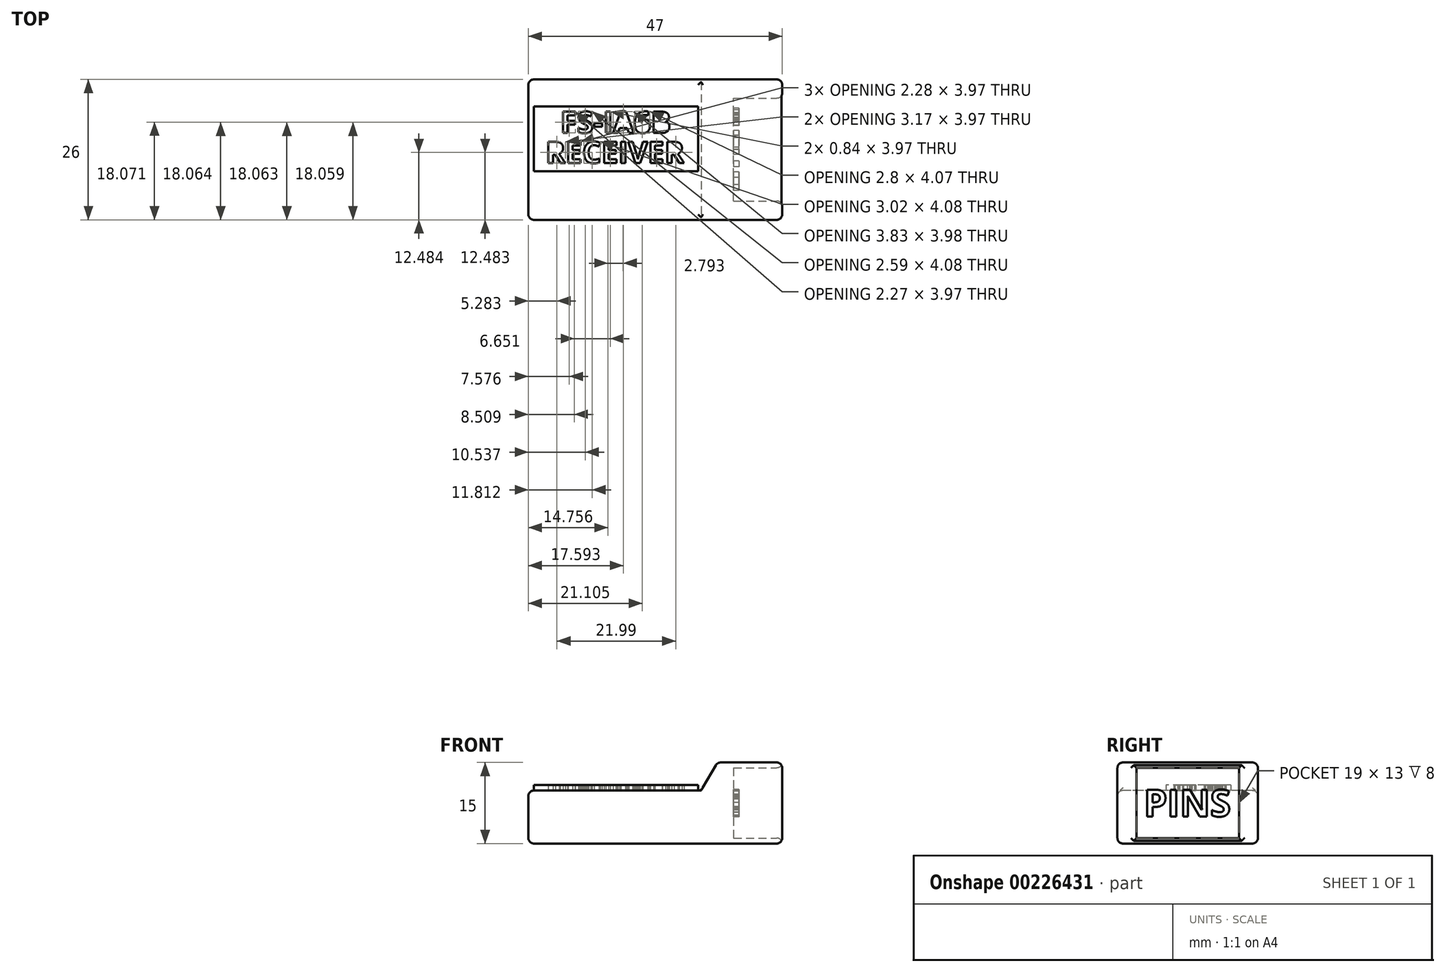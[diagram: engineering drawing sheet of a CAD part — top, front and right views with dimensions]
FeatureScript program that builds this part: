
annotation { "Feature Type Name" : "Feature", "Feature Type Description" : "" }
export const myFeature = defineFeature(function(context is Context, id is Id, definition is map)
    precondition{}
    {
        {
            var Q0;
            Q0=qCreatedBy(makeId("Front.planeOp"),FACE);
            var sketch = newSketch(context, id + "F0", { "sketchPlane" : qUnion([Q0])});
            skLineSegment(sketch, "E0.bottom", {"start": v(0, 0) * mm, "end": v(47, 0) * mm});
            skLineSegment(sketch, "E0.top", {"start": v(0, -15) * mm, "end": v(47, -15) * mm});
            skLineSegment(sketch, "E0.left", {"start": v(0, 0) * mm, "end": v(0, -15) * mm});
            skLineSegment(sketch, "E0.right", {"start": v(47, 0) * mm, "end": v(47, -15) * mm});
            skSolve(sketch);
        }
        {
            var Q0;
            Q0=makeQuery(id+"F0.imprint","IMPRINT",FACE,{"disambiguationData":[TD([[makeQuery(id+"F0.imprint","IMPRINT",EDGE,{"derivedFrom":sQuery(id+"F0.wireOp",EDGE,"E0.bottom")}),-1.0]])]});
            extrude(context, id + "F1", {"entities" : qUnion([Q0]), "depth" : 26 * mm, "offsetDistance" : 25.4 * mm});
        }
        {
            var Q0;
            Q0=makeQuery(id+"F1.opExtrude","CAP_FACE",FACE,{"disambiguationData":[OSD([sQuery(id+"F0.wireOp",EDGE,"E0.bottom"),sQuery(id+"F0.wireOp",EDGE,"E0.top"),sQuery(id+"F0.wireOp",EDGE,"E0.left"),sQuery(id+"F0.wireOp",EDGE,"E0.right")])],"isStart":false});
            var sketch = newSketch(context, id + "F2", { "sketchPlane" : qUnion([Q0])});
            skLineSegment(sketch, "E1", {"start": v(0, -5.2) * mm, "end": v(32, -5.2) * mm});
            skLineSegment(sketch, "E2", {"start": v(32, -5.2) * mm, "end": v(35, 0) * mm});
            skSolve(sketch);
        }
        {
            var Q0;
            {var subQ0=sQuery(id+"F2.wireOp",EDGE,"E1");Q0=makeQuery(id+"F2.imprint","IMPRINT",FACE,{"disambiguationData":[TD([[makeQuery(id+"F2.imprint","IMPRINT",EDGE,{"derivedFrom":subQ0}),1.0]])]});}
            extrude(context, id + "F3", {"entities" : qUnion([Q0]), "operationType" : NewBodyOperationType.REMOVE, "endBound" : BoundingType.THROUGH_ALL, "oppositeDirection" : true, "depth" : 25.4 * mm, "offsetDistance" : 25.4 * mm});
        }
        {
            var Q0;
            Q0=makeQuery(id+"F1.opExtrude","SWEPT_FACE",FACE,{"disambiguationData":[OSD([sQuery(id+"F0.wireOp",EDGE,"E0.right")])]});
            var sketch = newSketch(context, id + "F4", { "sketchPlane" : qUnion([Q0])});
            skLineSegment(sketch, "E3.bottom", {"start": v(-22.5, -1) * mm, "end": v(-3.5, -1) * mm});
            skLineSegment(sketch, "E3.top", {"start": v(-22.5, -14) * mm, "end": v(-3.5, -14) * mm});
            skLineSegment(sketch, "E3.left", {"start": v(-22.5, -1) * mm, "end": v(-22.5, -14) * mm});
            skLineSegment(sketch, "E3.right", {"start": v(-3.5, -1) * mm, "end": v(-3.5, -14) * mm});
            skLineSegment(sketch, "E4", {"start": v(-16.92, -1) * mm, "end": v(-16.92, 0) * mm});
            skLineSegment(sketch, "E5", {"start": v(-3.5, -5.73) * mm, "end": v(0, -5.73) * mm});
            skLineSegment(sketch, "E6", {"start": v(-8.9, -14) * mm, "end": v(-8.9, -15) * mm});
            skLineSegment(sketch, "E7", {"start": v(-22.5, -9.4) * mm, "end": v(-26, -9.4) * mm});
            skSolve(sketch);
        }
        {
            var Q0;
            {var subQ4=sQuery(id+"F4.wireOp",EDGE,"E3.left");var subQ6=sQuery(id+"F4.wireOp",EDGE,"E3.bottom");var subQ9=makeQuery(id+"F4.imprint","INTERSECT",VERTEX,{"derivedFrom":[subQ6,subQ4]});Q0=makeQuery(id+"F4.imprint","IMPRINT",FACE,{"disambiguationData":[TD([[makeQuery(id+"F4.imprint","IMPRINT",EDGE,{"disambiguationData":[TD([[subQ9,-1.0]])],"derivedFrom":subQ6}),-1.0]])]});}
            extrude(context, id + "F5", {"entities" : qUnion([Q0]), "operationType" : NewBodyOperationType.REMOVE, "oppositeDirection" : true, "depth" : 9 * mm, "offsetDistance" : 25.4 * mm});
        }
        {
            var Q0;
            Q0=makeQuery(id+"F5.boolean.opBoolean","COPY",FACE,{"derivedFrom":makeQuery(id+"F5.opExtrude","CAP_FACE",FACE,{"disambiguationData":[OSD([sQuery(id+"F4.wireOp",EDGE,"E3.bottom"),sQuery(id+"F4.wireOp",EDGE,"E3.top"),sQuery(id+"F4.wireOp",EDGE,"E3.left"),sQuery(id+"F4.wireOp",EDGE,"E3.right")])],"isStart":false})});
            var sketch = newSketch(context, id + "F6", { "sketchPlane" : qUnion([Q0])});
            skText(sketch, "E8", { "text": "PINS", "fontName": "OpenSans-Bold.ttf"});
            skLineSegment(sketch, "E9", {"start": v(-13, -5) * mm, "end": v(-13, -1) * mm});
            skLineSegment(sketch, "E10", {"start": v(-13, -10) * mm, "end": v(-13, -14) * mm});
            skLineSegment(sketch, "E11", {"start": v(-4.85, -6.78) * mm, "end": v(-3.5, -6.78) * mm});
            skLineSegment(sketch, "E12", {"start": v(-21.15, -6.7) * mm, "end": v(-22.5, -6.7) * mm});
            const initialGuessF6  = {"E8": [-0.02115, -0.01, 1, 0, 0.005]};
            skSetInitialGuess(sketch, initialGuessF6);
            skSolve(sketch);
        }
        {
            var Q0;
            Q0 = qSketchRegion(id + "F6", true);
            extrude(context, id + "F7", {"entities" : qUnion([Q0]), "depth" : 1 * mm, "offsetDistance" : 25.4 * mm});
        }
        {
            var Q0;
            Q0=makeQuery(id+"F3.boolean.opBoolean","COPY",FACE,{"derivedFrom":makeQuery(id+"F3.opExtrude","SWEPT_FACE",FACE,{"disambiguationData":[OSD([sQuery(id+"F2.wireOp",EDGE,"E1")])]})});
            var Q1;
            Q1=makeQuery(id+"F1.opExtrude","SWEPT_FACE",FACE,{"disambiguationData":[OSD([sQuery(id+"F0.wireOp",EDGE,"E0.left")])]});
            var Q2;
            Q2=makeQuery(id+"F1.opExtrude","CAP_FACE",FACE,{"disambiguationData":[OSD([sQuery(id+"F0.wireOp",EDGE,"E0.bottom"),sQuery(id+"F0.wireOp",EDGE,"E0.top"),sQuery(id+"F0.wireOp",EDGE,"E0.left"),sQuery(id+"F0.wireOp",EDGE,"E0.right")])],"isStart":true});
            var Q3;
            Q3=makeQuery(id+"F1.opExtrude","SWEPT_FACE",FACE,{"disambiguationData":[OSD([sQuery(id+"F0.wireOp",EDGE,"E0.right")])]});
            var Q4;
            Q4=makeQuery(id+"F1.opExtrude","SWEPT_FACE",FACE,{"disambiguationData":[OSD([sQuery(id+"F0.wireOp",EDGE,"E0.bottom")])]});
            var Q5;
            Q5=makeQuery(id+"F1.opExtrude","SWEPT_FACE",FACE,{"disambiguationData":[OSD([sQuery(id+"F0.wireOp",EDGE,"E0.top")])]});
            var Q6;
            Q6=makeQuery(id+"F1.opExtrude","CAP_FACE",FACE,{"disambiguationData":[OSD([sQuery(id+"F0.wireOp",EDGE,"E0.bottom"),sQuery(id+"F0.wireOp",EDGE,"E0.top"),sQuery(id+"F0.wireOp",EDGE,"E0.left"),sQuery(id+"F0.wireOp",EDGE,"E0.right")])],"isStart":false});
            fillet(context, id + "F8", {"entities" : qUnion([Q0, Q1, Q2, Q3, Q4, Q5, Q6]), "radius" : 1 * mm, "tangentPropagation" : true, "allowEdgeOverflow" : false});
        }
        {
            var Q0;
            Q0=makeQuery(id+"F3.boolean.opBoolean","COPY",FACE,{"derivedFrom":makeQuery(id+"F3.opExtrude","SWEPT_FACE",FACE,{"disambiguationData":[OSD([sQuery(id+"F2.wireOp",EDGE,"E1")])]})});
            var sketch = newSketch(context, id + "F9", { "sketchPlane" : qUnion([Q0])});
            skText(sketch, "E13", { "text": "FS-IA6B ", "fontName": "OpenSans-Bold.ttf"});
            skText(sketch, "E14", { "text": "RECEIVER\n", "fontName": "OpenSans-Bold.ttf"});
            skLineSegment(sketch, "E15", {"start": v(20.93, -1) * mm, "end": v(20.93, -5.92) * mm});
            skLineSegment(sketch, "E16", {"start": v(18.81, -9.92) * mm, "end": v(18.81, -25) * mm});
            skLineSegment(sketch, "E17", {"start": v(26.48, -7.92) * mm, "end": v(31.42, -7.92) * mm});
            skLineSegment(sketch, "E18", {"start": v(5.94, -7.92) * mm, "end": v(1, -7.92) * mm});
            skLineSegment(sketch, "E19", {"start": v(3.2, -15.49) * mm, "end": v(1, -15.49) * mm});
            skLineSegment(sketch, "E20", {"start": v(29.22, -13.5) * mm, "end": v(31.42, -13.5) * mm});
            skLineSegment(sketch, "E21.bottom", {"start": v(1, -5) * mm, "end": v(31.42, -5) * mm});
            skLineSegment(sketch, "E21.top", {"start": v(1, -17) * mm, "end": v(31.42, -17) * mm});
            skLineSegment(sketch, "E21.left", {"start": v(1, -5) * mm, "end": v(1, -17) * mm});
            skLineSegment(sketch, "E21.right", {"start": v(31.42, -5) * mm, "end": v(31.42, -17) * mm});
            const initialGuessF9  = {"E13": [0.00594, -0.00992, 1, 0, 0.004], "E14": [0.0032, -0.0155, 1, 0, 0.004]};
            skSetInitialGuess(sketch, initialGuessF9);
            skSolve(sketch);
        }
        {
            var Q0;
            Q0 = qSketchRegion(id + "F9", true);
            extrude(context, id + "F10", {"entities" : qUnion([Q0]), "depth" : 1 * mm, "offsetDistance" : 25.4 * mm});
        }
    });
